# Revit family: QF_Brema_DSS42A_DSS42W_cat
name_source: partatom
category: Specialty Equipment
revit_build: Autodesk Revit MEP 2012 (Build: 20110916_2132(x64)
units: mm (PartAtom-declared; Revit-internal decimal feet)

## types (2) — shared parameters
Apparent Power = 450 VA
Assembly Code = E1090320
BTUH = 0 W
Cold Water Maximum Pressure = 6.0 bar
Cold Water Minimum Pressure = 1.0 bar
Cold Water Size = 1"
Cold Water Size Radius = 1/2"
Conn Conduit = Yes
Cycle = 50 Hz
Depth = 630 mm  [stored 2.06693 ft]
Elec Conn Connection Height = 347 mm  [stored 1.13845 ft]
FL Amps = 0 A
Height = 920 mm  [stored 3.01837 ft]
Indirect Waste Connection Height = 270 mm  [stored 0.885827 ft]
Indirect Waste Radius = 1/2"
Indirect Waste Size = 1"
Manufacturer = BREMA
Max Overcurrent Protection = 10 A
Min Ckt Ampacity = 0 A
Phase = 1
Refrigerant Type = R404A
URL = www.bremaice.it
Volts = 230 V
Watts = 450 W
Weight = 66 kg
Width = 500 mm  [stored 1.64042 ft]

## per-type parameters (varying)
| type | Cold Water Connection Height | Description |
| DSS42A | 270 mm  [stored 0.885827 ft] | AUTOMATIC ICE CUBE MAKER AIR COOLED |
| DSS42W | 311 mm  [stored 1.02034 ft] | AUTOMATIC ICE CUBE MAKER WATER COOLED |

note: column(s) folded — value = type name in every type: Model

note: [stored X ft] marks values corroborated as IEEE doubles in the binary element streams (Revit-internal decimal feet)

## geometry (parser evidence)
native form markers: Blend x10, Sweep x2
no freeform markers — native parametric forms only
